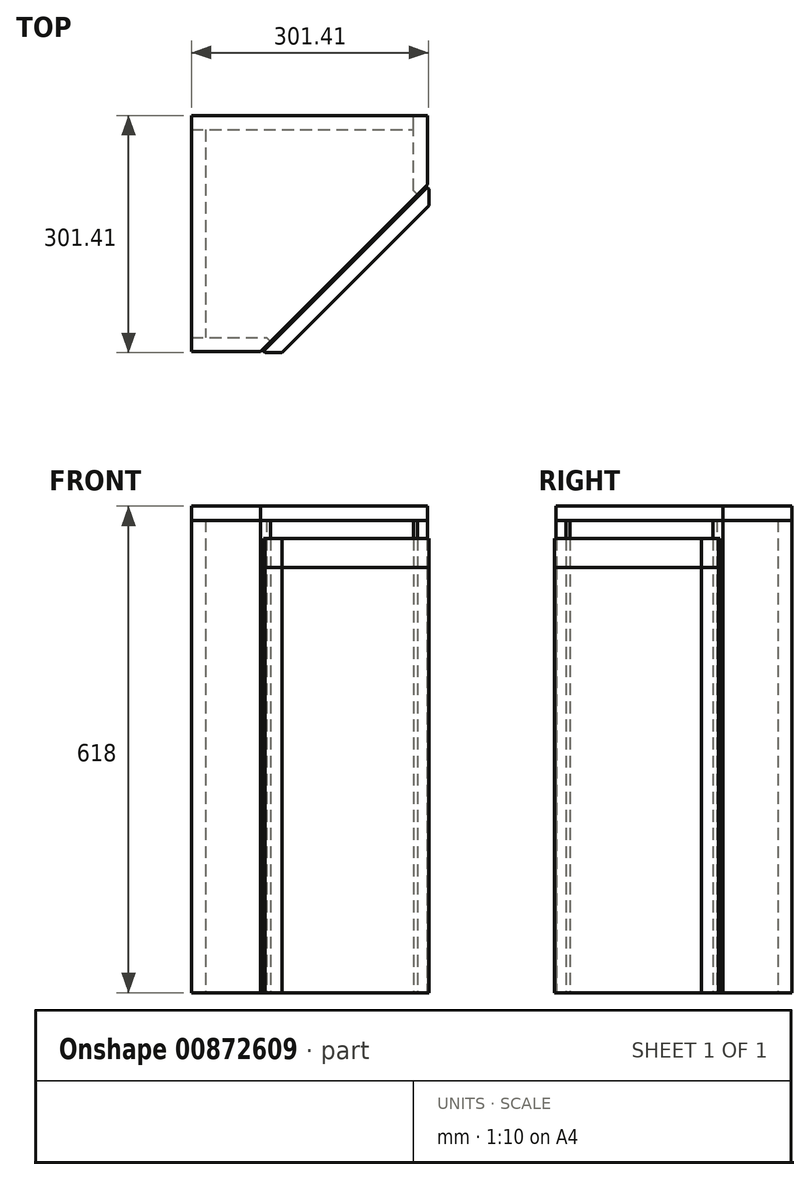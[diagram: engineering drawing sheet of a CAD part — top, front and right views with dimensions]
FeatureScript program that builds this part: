
annotation { "Feature Type Name" : "Feature", "Feature Type Description" : "" }
export const myFeature = defineFeature(function(context is Context, id is Id, definition is map)
    precondition{}
    {
        {
            var Q0;
            Q0=qCreatedBy(makeId("Top.planeOp"),FACE);
            var sketch = newSketch(context, id + "F0", { "sketchPlane" : qUnion([Q0])});
            skLineSegment(sketch, "E0.bottom", {"start": v(0, 0) * mm, "end": v(18, 0) * mm});
            skLineSegment(sketch, "E0.top", {"start": v(0, -264) * mm, "end": v(18, -264) * mm});
            skLineSegment(sketch, "E0.left", {"start": v(0, 0) * mm, "end": v(0, -264) * mm});
            skLineSegment(sketch, "E0.right", {"start": v(18, 0) * mm, "end": v(18, -264) * mm});
            skLineSegment(sketch, "E1.bottom", {"start": v(0, 0) * mm, "end": v(282, 0) * mm});
            skLineSegment(sketch, "E1.top", {"start": v(0, 18) * mm, "end": v(282, 18) * mm});
            skLineSegment(sketch, "E1.left", {"start": v(0, 0) * mm, "end": v(0, 18) * mm});
            skLineSegment(sketch, "E1.right", {"start": v(282, 0) * mm, "end": v(282, 18) * mm});
            skLineSegment(sketch, "E2.bottom", {"start": v(0, -264) * mm, "end": v(105.87, -264) * mm});
            skLineSegment(sketch, "E2.top", {"start": v(0, -282) * mm, "end": v(87.87, -282) * mm});
            skLineSegment(sketch, "E2.left", {"start": v(0, -264) * mm, "end": v(0, -282) * mm});
            skLineSegment(sketch, "E3.bottom", {"start": v(282, 18) * mm, "end": v(300, 18) * mm});
            skLineSegment(sketch, "E3.left", {"start": v(282, 18) * mm, "end": v(282, -87.87) * mm});
            skLineSegment(sketch, "E3.right", {"start": v(300, 18) * mm, "end": v(300, -69.87) * mm});
            skLineSegment(sketch, "E4", {"start": v(102.01, -296.14) * mm, "end": v(314.14, -84.01) * mm});
            skLineSegment(sketch, "E5", {"start": v(102.01, -296.14) * mm, "end": v(89.28, -283.41) * mm});
            skLineSegment(sketch, "E6", {"start": v(314.14, -84.01) * mm, "end": v(301.41, -71.28) * mm});
            skLineSegment(sketch, "E7", {"start": v(301.41, -71.28) * mm, "end": v(89.28, -283.41) * mm});
            skLineSegment(sketch, "E8", {"start": v(87.87, -282) * mm, "end": v(105.87, -264) * mm});
            skLineSegment(sketch, "E9", {"start": v(300, -69.87) * mm, "end": v(282, -87.87) * mm});
            skLineSegment(sketch, "E10", {"start": v(301.41, -71.28) * mm, "end": v(300, -69.87) * mm, "construction": true});
            skLineSegment(sketch, "E11", {"start": v(105.87, -300) * mm, "end": v(89.28, -283.41) * mm, "construction": true});
            skLineSegment(sketch, "E12", {"start": v(95.32, -264) * mm, "end": v(100.6, -269.27) * mm});
            skLineSegment(sketch, "E13", {"start": v(282, -77.32) * mm, "end": v(287.27, -82.6) * mm});
            skLineSegment(sketch, "E14", {"start": v(301.41, -71.28) * mm, "end": v(301.41, -96.74) * mm});
            skLineSegment(sketch, "E15", {"start": v(89.28, -283.41) * mm, "end": v(114.74, -283.41) * mm});
            skLineSegment(sketch, "E16", {"start": v(91.4, -281.3) * mm, "end": v(93.52, -283.41) * mm});
            skLineSegment(sketch, "E17", {"start": v(299.3, -73.4) * mm, "end": v(301.41, -75.52) * mm});
            skSolve(sketch);
        }
        {
            var Q0;
            {var subQ0=sQuery(id+"F0.wireOp",EDGE,"E0.left");Q0=makeQuery(id+"F0.imprint","IMPRINT",FACE,{"disambiguationData":[TD([[makeQuery(id+"F0.imprint","IMPRINT",EDGE,{"derivedFrom":subQ0}),1.0]])]});}
            extrude(context, id + "F1", {"entities" : qUnion([Q0]), "depth" : 600 * mm, "offsetDistance" : 25 * mm});
        }
        {
            var Q0;
            {var subQ1=sQuery(id+"F0.wireOp",EDGE,"E1.top");Q0=makeQuery(id+"F0.imprint","IMPRINT",FACE,{"disambiguationData":[TD([[makeQuery(id+"F0.imprint","IMPRINT",EDGE,{"derivedFrom":subQ1}),-1.0]])]});}
            extrude(context, id + "F2", {"entities" : qUnion([Q0]), "depth" : 600 * mm, "offsetDistance" : 25 * mm});
        }
        {
            var Q0;
            {var subQ0=sQuery(id+"F0.wireOp",EDGE,"E2.left");Q0=makeQuery(id+"F0.imprint","IMPRINT",FACE,{"disambiguationData":[TD([[makeQuery(id+"F0.imprint","IMPRINT",EDGE,{"derivedFrom":subQ0}),1.0]])]});}
            var Q1;
            {var subQ1=sQuery(id+"F0.wireOp",EDGE,"E3.bottom");Q1=makeQuery(id+"F0.imprint","IMPRINT",FACE,{"disambiguationData":[TD([[makeQuery(id+"F0.imprint","IMPRINT",EDGE,{"derivedFrom":subQ1}),-1.0]])]});}
            extrude(context, id + "F3", {"entities" : qUnion([Q0, Q1]), "depth" : 600 * mm, "offsetDistance" : 25 * mm});
        }
        {
            var Q0;
            {var subQ3=sQuery(id+"F0.wireOp",EDGE,"E16");Q0=makeQuery(id+"F0.imprint","IMPRINT",FACE,{"disambiguationData":[TD([[makeQuery(id+"F0.imprint","IMPRINT",EDGE,{"derivedFrom":subQ3}),1.0]])]});}
            extrude(context, id + "F4", {"entities" : qUnion([Q0]), "depth" : 540 * mm, "offsetDistance" : 25 * mm});
        }
        {
            var Q0;
            Q0=makeQuery(id+"F1.opExtrude","CAP_FACE",FACE,{"disambiguationData":[OSD([sQuery(id+"F0.wireOp",EDGE,"E0.left"),sQuery(id+"F0.wireOp",EDGE,"E0.right"),sQuery(id+"F0.wireOp",EDGE,"E1.bottom"),sQuery(id+"F0.wireOp",EDGE,"E2.bottom")])],"isStart":false});
            var sketch = newSketch(context, id + "F5", { "sketchPlane" : qUnion([Q0])});
            skLineSegment(sketch, "E18.0", {"start": v(0, -282) * mm, "end": v(0, -282) * mm});
            skLineSegment(sketch, "E18.1", {"start": v(0, -264) * mm, "end": v(0, -282) * mm});
            skLineSegment(sketch, "E18.2", {"start": v(0, 0) * mm, "end": v(0, -264) * mm});
            skLineSegment(sketch, "E18.3", {"start": v(0, 0) * mm, "end": v(0, 18) * mm});
            skLineSegment(sketch, "E18.4", {"start": v(0, 18) * mm, "end": v(282, 18) * mm});
            skLineSegment(sketch, "E18.5", {"start": v(282, 18) * mm, "end": v(300, 18) * mm});
            skLineSegment(sketch, "E18.6", {"start": v(300, 18) * mm, "end": v(300, 18) * mm});
            skLineSegment(sketch, "E19.0", {"start": v(300, 18) * mm, "end": v(300, -69.87) * mm});
            skLineSegment(sketch, "E19.1", {"start": v(0, -282) * mm, "end": v(87.87, -282) * mm});
            skLineSegment(sketch, "E20", {"start": v(87.87, -282) * mm, "end": v(300, -69.87) * mm});
            skSolve(sketch);
        }
        {
            var Q0;
            Q0 = qSketchRegion(id + "F5", true);
            extrude(context, id + "F6", {"entities" : qUnion([Q0]), "depth" : 18 * mm, "offsetDistance" : 25 * mm});
        }
        {
            var Q0;
            Q0=makeQuery(id+"F4.opExtrude","CAP_FACE",FACE,{"disambiguationData":[OSD([sQuery(id+"F0.wireOp",EDGE,"E4"),sQuery(id+"F0.wireOp",EDGE,"E7"),sQuery(id+"F0.wireOp",EDGE,"E14"),sQuery(id+"F0.wireOp",EDGE,"E15"),sQuery(id+"F0.wireOp",EDGE,"E16"),sQuery(id+"F0.wireOp",EDGE,"E17")])],"isStart":false});
            extrude(context, id + "F7", {"entities" : qUnion([Q0]), "depth" : ((78 / 2) - 2) * mm, "offsetDistance" : 25 * mm});
        }
    });
